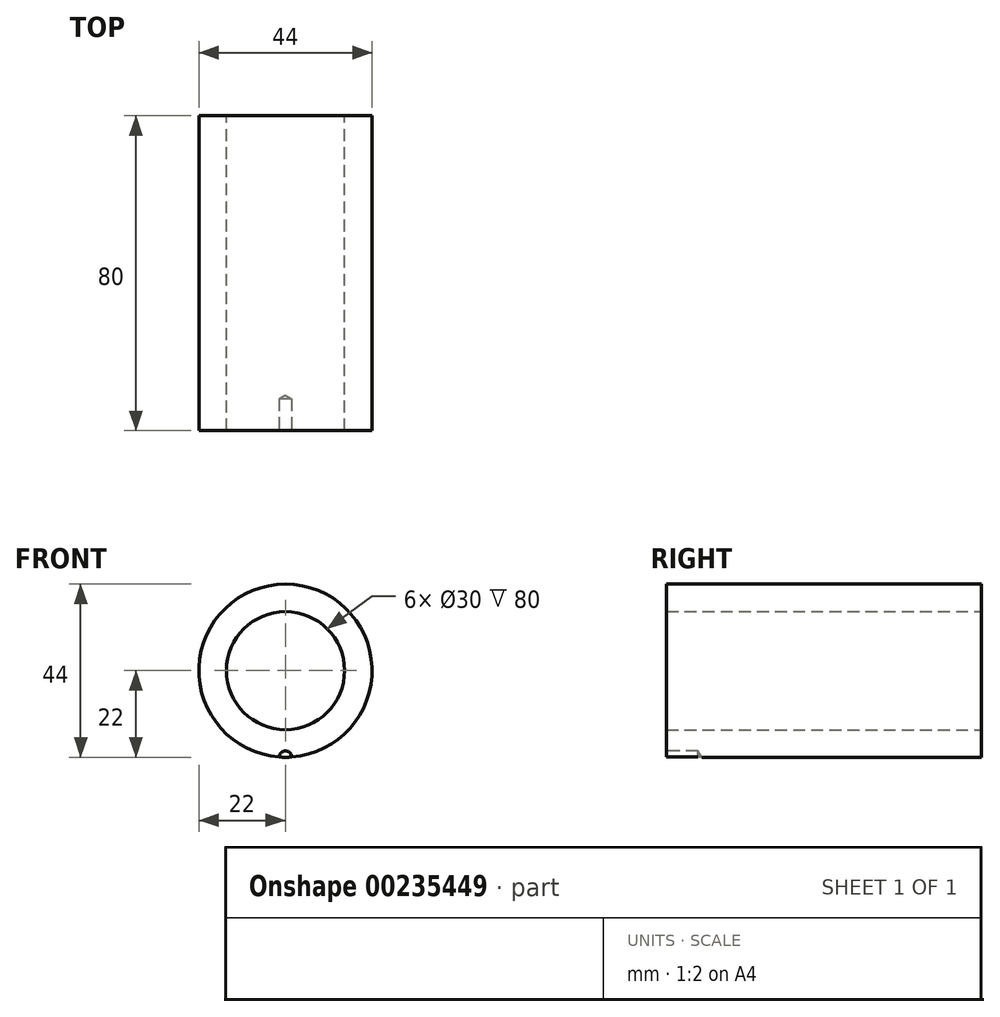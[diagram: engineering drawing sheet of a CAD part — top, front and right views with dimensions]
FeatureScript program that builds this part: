
annotation { "Feature Type Name" : "Feature", "Feature Type Description" : "" }
export const myFeature = defineFeature(function(context is Context, id is Id, definition is map)
    precondition{}
    {
        {
            var Q0;
            Q0=qCreatedBy(makeId("Front.planeOp"),FACE);
            var sketch = newSketch(context, id + "F0", { "sketchPlane" : qUnion([Q0])});
            skCircle(sketch, "E0", {"center": v(0, 0) * mm, "radius": 22 * mm});
            skCircle(sketch, "E1", {"center": v(0, 0) * mm, "radius": 15 * mm});
            skSolve(sketch);
        }
        {
            var Q0;
            Q0 = qSketchRegion(id + "F0", true);
            extrude(context, id + "F1", {"entities" : qUnion([Q0]), "depth" : 40 * mm, "hasSecondDirection" : true, "secondDirectionOppositeDirection" : true, "secondDirectionDepth" : 40 * mm});
        }
        {
            var Q0;
            Q0=makeQuery(id+"F1.opExtrude","CAP_FACE",FACE,{"disambiguationData":[OSD([sQuery(id+"F0.wireOp",EDGE,"E0"),sQuery(id+"F0.wireOp",EDGE,"E1")])],"isStart":false});
            var sketch = newSketch(context, id + "F2", { "sketchPlane" : qUnion([Q0])});
            skPoint(sketch, "E2", {"position": v(0, -22) * mm});
            skSolve(sketch);
        }
        {
            var Q0;
            Q0=sQuery(id+"F2.wireOp",VERTEX,"E2");
            var Q1;
            Q1=makeQuery(id+"F1.opExtrude","SWEPT_BODY",BODY,{"disambiguationData":[OSD([sQuery(id+"F0.wireOp",EDGE,"E0"),sQuery(id+"F0.wireOp",EDGE,"E1")])]});
            hole(context, id + "F3", {"style" : HoleStyle.SIMPLE, "endStyle" : HoleEndStyle.BLIND, "standardTappedOrClearance" : lookupTablePath({ "standard" : "ISO", "fit" : "Normal", "engagement" : "75%", "pitch" : "0.75 mm", "size" : "M4", "type" : "Tapped" }), "standardBlindInLast" : lookupTablePath({ "fit" : "Standard", "standard" : "ISO", "engagement" : "75%", "pitch" : "0.75 mm", "size" : "M4", "type" : "Tapped" }), "holeDiameter" : 3.2 * mm, "holeDepth" : 8 * mm, "locations" : qUnion([Q0]), "scope" : qUnion([Q1])});
        }
    });
